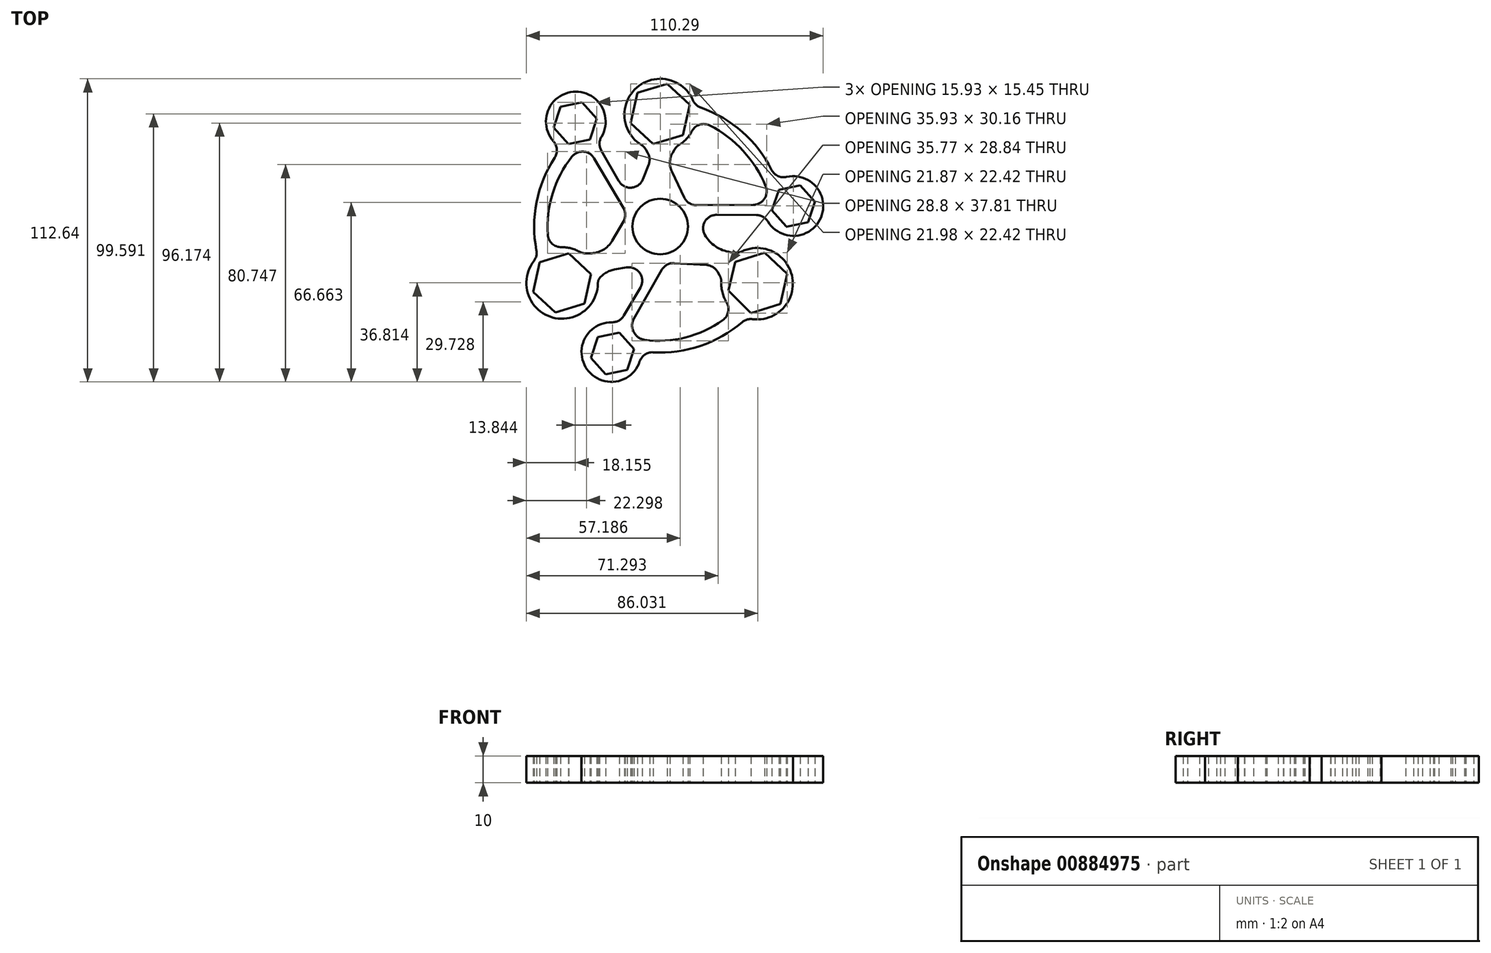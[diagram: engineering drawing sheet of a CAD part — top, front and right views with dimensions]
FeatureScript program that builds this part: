
annotation { "Feature Type Name" : "Feature", "Feature Type Description" : "" }
export const myFeature = defineFeature(function(context is Context, id is Id, definition is map)
    precondition{}
    {
        {
            var Q0;
            Q0=qCreatedBy(makeId("Top.planeOp"),FACE);
            var sketch = newSketch(context, id + "F0", { "sketchPlane" : qUnion([Q0])});
            skCircle(sketch, "E0", {"center": v(0, 0) * mm, "radius": 10.34 * mm});
            skLineSegment(sketch, "E1", {"start": v(16.56, -3.08) * mm, "end": v(16.6, -3.15) * mm});
            skLineSegment(sketch, "E2", {"start": v(21.4, -16.95) * mm, "end": v(22.04, -18.04) * mm});
            skLineSegment(sketch, "E3.1.0", {"start": v(4.6, 27.4) * mm, "end": v(5.25, 28.52) * mm});
            skLineSegment(sketch, "E3.1.1", {"start": v(-6.37, 17.62) * mm, "end": v(-4.26, 23.1) * mm});
            skLineSegment(sketch, "E3.2.0", {"start": v(-26.02, -9.98) * mm, "end": v(-27.6, -9.98) * mm});
            skLineSegment(sketch, "E3.2.1", {"start": v(-12.57, -15.21) * mm, "end": v(-16.95, -16) * mm});
            skLineSegment(sketch, "E4", {"start": v(0, -25.85) * mm, "end": v(0, -10.34) * mm, "construction": true});
            skLineSegment(sketch, "E5.MirrorCS", {"start": v(-13.7, 1.87) * mm, "end": v(-17.8, -5.24) * mm});
            skLineSegment(sketch, "E6.1.0", {"start": v(26.05, -9.53) * mm, "end": v(27.33, -9.72) * mm});
            skLineSegment(sketch, "E6.1.1", {"start": v(5.2, -13.6) * mm, "end": v(17.15, -14.32) * mm});
            skLineSegment(sketch, "E6.2.0", {"start": v(-4.6, 27.4) * mm, "end": v(-5.25, 28.52) * mm});
            skLineSegment(sketch, "E6.2.1", {"start": v(8.96, 10.77) * mm, "end": v(4.33, 20.43) * mm});
            skPoint(sketch, "E7", {"position": v(2.46, 10.04) * mm});
            skPoint(sketch, "E8", {"position": v(-2.46, 10.04) * mm});
            skPoint(sketch, "E9", {"position": v(7.46, 7.15) * mm});
            skPoint(sketch, "E10", {"position": v(9.92, 2.9) * mm});
            skPoint(sketch, "E11", {"position": v(-7.46, 7.15) * mm});
            skPoint(sketch, "E12", {"position": v(-9.92, 2.9) * mm});
            skPoint(sketch, "E13", {"position": v(9.92, -2.9) * mm});
            skPoint(sketch, "E14", {"position": v(7.46, -7.15) * mm});
            skPoint(sketch, "E15", {"position": v(-7.46, -7.15) * mm});
            skPoint(sketch, "E16", {"position": v(-9.92, -2.9) * mm});
            skPoint(sketch, "E17", {"position": v(-2.46, 4.26) * mm});
            skPoint(sketch, "E18", {"position": v(2.46, 4.26) * mm});
            skPoint(sketch, "E19", {"position": v(2.46, -4.26) * mm});
            skPoint(sketch, "E20", {"position": v(-2.46, -4.26) * mm});
            skPoint(sketch, "E21", {"position": v(-4.92, 0) * mm});
            skPoint(sketch, "E22", {"position": v(4.92, 0) * mm});
            skPoint(sketch, "E23", {"position": v(-2.46, 5.46) * mm});
            skPoint(sketch, "E24", {"position": v(2.46, 5.46) * mm});
            skLineSegment(sketch, "E25.2.0", {"start": v(0.55, -16.12) * mm, "end": v(-9.8, -34.32) * mm});
            skLineSegment(sketch, "E25.2.1", {"start": v(-7.37, -22.66) * mm, "end": v(-13.47, -33.1) * mm});
            skLineSegment(sketch, "E26.trimOffspring", {"start": v(0, 10.34) * mm, "end": v(0, 30.35) * mm, "construction": true});
            skPoint(sketch, "E27.third.point", {"position": v(-26.64, -15.38) * mm});
            skPoint(sketch, "E28.third.point", {"position": v(0, 30.35) * mm});
            skPoint(sketch, "E29.third.point", {"position": v(26.28, -15.18) * mm});
            skPoint(sketch, "E30.end.orphan", {"position": v(-26.74, -20.71) * mm});
            skPoint(sketch, "E31.orphan", {"position": v(31.3, -15.18) * mm});
            skPoint(sketch, "E32.orphan", {"position": v(26.74, -20.71) * mm});
            skPoint(sketch, "E33.orphan", {"position": v(-2.51, 34.7) * mm});
            skLineSegment(sketch, "E34.0", {"start": v(-28.18, -28.67) * mm, "end": v(-38.97, -32) * mm});
            skLineSegment(sketch, "E34.1", {"start": v(-38.97, -32) * mm, "end": v(-47.24, -24.3) * mm});
            skLineSegment(sketch, "E34.2", {"start": v(-47.24, -24.3) * mm, "end": v(-44.71, -13.3) * mm});
            skLineSegment(sketch, "E34.3", {"start": v(-44.71, -13.3) * mm, "end": v(-33.92, -9.98) * mm});
            skLineSegment(sketch, "E34.4", {"start": v(-33.92, -9.98) * mm, "end": v(-25.65, -17.67) * mm});
            skLineSegment(sketch, "E34.5", {"start": v(-25.65, -17.67) * mm, "end": v(-28.18, -28.67) * mm});
            skLineSegment(sketch, "E35.1.0", {"start": v(33.67, -32.13) * mm, "end": v(25.37, -23.8) * mm});
            skLineSegment(sketch, "E35.1.1", {"start": v(25.37, -23.8) * mm, "end": v(27.82, -13.1) * mm});
            skLineSegment(sketch, "E35.1.2", {"start": v(27.82, -13.1) * mm, "end": v(38.81, -9.72) * mm});
            skLineSegment(sketch, "E35.1.3", {"start": v(38.81, -9.72) * mm, "end": v(47.24, -17.55) * mm});
            skLineSegment(sketch, "E35.1.4", {"start": v(47.24, -17.55) * mm, "end": v(44.67, -28.76) * mm});
            skLineSegment(sketch, "E35.1.5", {"start": v(44.67, -28.76) * mm, "end": v(33.67, -32.13) * mm});
            skLineSegment(sketch, "E35.2.0", {"start": v(11, 45.23) * mm, "end": v(8.42, 34.02) * mm});
            skLineSegment(sketch, "E35.2.1", {"start": v(8.42, 34.02) * mm, "end": v(-2.57, 30.64) * mm});
            skLineSegment(sketch, "E35.2.2", {"start": v(-2.57, 30.64) * mm, "end": v(-11, 38.47) * mm});
            skLineSegment(sketch, "E35.2.3", {"start": v(-11, 38.47) * mm, "end": v(-8.42, 49.68) * mm});
            skLineSegment(sketch, "E35.2.4", {"start": v(-8.42, 49.68) * mm, "end": v(2.57, 53.06) * mm});
            skLineSegment(sketch, "E35.2.5", {"start": v(2.57, 53.06) * mm, "end": v(11, 45.23) * mm});
            skArc(sketch, "E36.0", {"start": v(-30.01, -9.36) * mm, "mid": v(-33.24, -8.1) * mm, "end": v(-36.68, -7.7) * mm});
            skArc(sketch, "E37.1.0", {"start": v(22.7, -20.74) * mm, "mid": v(23.12, -24.58) * mm, "end": v(24.62, -28.14) * mm});
            skArc(sketch, "E37.2.0", {"start": v(6.96, 30.28) * mm, "mid": v(9.71, 32.53) * mm, "end": v(11.77, 35.43) * mm});
            skPoint(sketch, "E37.center", {"position": v(-0.15, -0.21) * mm});
            skPoint(sketch, "E38.orphan", {"position": v(28.18, -28.67) * mm});
            skArc(sketch, "E39.filletArc", {"start": v(-4.26, 23.1) * mm, "mid": v(-3.94, 25.28) * mm, "end": v(-4.6, 27.4) * mm});
            skArc(sketch, "E40.filletArc", {"start": v(4.6, 27.4) * mm, "mid": v(3.6, 23.95) * mm, "end": v(4.33, 20.43) * mm});
            skArc(sketch, "E41.filletArc", {"start": v(16.56, -3.08) * mm, "mid": v(20.57, -7.4) * mm, "end": v(26.05, -9.53) * mm});
            skPoint(sketch, "E42.newPointB", {"position": v(14.67, -5.29) * mm});
            skArc(sketch, "E42.filletArc", {"start": v(21.4, -16.95) * mm, "mid": v(19.6, -15.1) * mm, "end": v(17.15, -14.32) * mm});
            skPoint(sketch, "E43.newPointA", {"position": v(-14.67, -5.29) * mm});
            skArc(sketch, "E43.filletArc", {"start": v(-16.95, -16) * mm, "mid": v(-20.24, -17.25) * mm, "end": v(-22.86, -19.61) * mm});
            skArc(sketch, "E44.filletArc", {"start": v(-26.02, -9.98) * mm, "mid": v(-21.28, -8.71) * mm, "end": v(-17.8, -5.24) * mm});
            skPoint(sketch, "E45.orphan", {"position": v(6.09, -6.37) * mm});
            skLineSegment(sketch, "E46.1.0", {"start": v(20.95, 4.35) * mm, "end": v(35.75, 4.28) * mm});
            skLineSegment(sketch, "E46.1.1", {"start": v(13.5, 7.93) * mm, "end": v(34.59, 8.08) * mm});
            skLineSegment(sketch, "E46.2.0", {"start": v(-15.38, 16.94) * mm, "end": v(-21.87, 28.32) * mm});
            skLineSegment(sketch, "E46.2.1", {"start": v(-13.72, 6.9) * mm, "end": v(-24.56, 25.37) * mm});
            skPoint(sketch, "E46.center", {"position": v(0.06, -0.37) * mm});
            skPoint(sketch, "E47.third.point", {"position": v(-38.87, 42.04) * mm});
            skLineSegment(sketch, "E48.0", {"start": v(-26.17, 32.36) * mm, "end": v(-34.13, 30.71) * mm});
            skLineSegment(sketch, "E48.1", {"start": v(-34.13, 30.71) * mm, "end": v(-39.54, 36.79) * mm});
            skLineSegment(sketch, "E48.2", {"start": v(-39.54, 36.79) * mm, "end": v(-36.98, 44.51) * mm});
            skLineSegment(sketch, "E48.3", {"start": v(-36.98, 44.51) * mm, "end": v(-29.02, 46.16) * mm});
            skLineSegment(sketch, "E48.4", {"start": v(-29.02, 46.16) * mm, "end": v(-23.6, 40.08) * mm});
            skLineSegment(sketch, "E48.5", {"start": v(-23.6, 40.08) * mm, "end": v(-26.17, 32.36) * mm});
            skLineSegment(sketch, "E49.1.0", {"start": v(-23.14, -41.09) * mm, "end": v(-15.17, -39.44) * mm});
            skLineSegment(sketch, "E49.1.1", {"start": v(-25.7, -48.81) * mm, "end": v(-23.14, -41.09) * mm});
            skLineSegment(sketch, "E49.1.2", {"start": v(-20.29, -54.89) * mm, "end": v(-25.7, -48.81) * mm});
            skLineSegment(sketch, "E49.1.3", {"start": v(-12.32, -53.24) * mm, "end": v(-20.29, -54.89) * mm});
            skLineSegment(sketch, "E49.1.4", {"start": v(-9.76, -45.52) * mm, "end": v(-12.32, -53.24) * mm});
            skLineSegment(sketch, "E49.1.5", {"start": v(-15.17, -39.44) * mm, "end": v(-9.76, -45.52) * mm});
            skLineSegment(sketch, "E49.2.0", {"start": v(46.92, -0.1) * mm, "end": v(41.51, 5.98) * mm});
            skLineSegment(sketch, "E49.2.1", {"start": v(54.89, 1.55) * mm, "end": v(46.92, -0.1) * mm});
            skLineSegment(sketch, "E49.2.2", {"start": v(57.45, 9.27) * mm, "end": v(54.89, 1.55) * mm});
            skLineSegment(sketch, "E49.2.3", {"start": v(52.04, 15.35) * mm, "end": v(57.45, 9.27) * mm});
            skLineSegment(sketch, "E49.2.4", {"start": v(44.07, 13.7) * mm, "end": v(52.04, 15.35) * mm});
            skLineSegment(sketch, "E49.2.5", {"start": v(41.51, 5.98) * mm, "end": v(44.07, 13.7) * mm});
            skArc(sketch, "E49.2.6", {"start": v(46.81, -0.06) * mm, "mid": v(46.87, -0.08) * mm, "end": v(46.92, -0.1) * mm});
            skArc(sketch, "E50.trimOffspring", {"start": v(46.81, -0.06) * mm, "mid": v(46.81, -0.02) * mm, "end": v(46.81, 0.02) * mm});
            skArc(sketch, "E51.trimOffspring", {"start": v(-2.6, -46.74) * mm, "mid": v(14.98, -44.35) * mm, "end": v(30.4, -35.6) * mm});
            skArc(sketch, "E52.trimOffspring", {"start": v(-5.84, -42.1) * mm, "mid": v(9.42, -41.24) * mm, "end": v(23.27, -34.78) * mm});
            skArc(sketch, "E53.trimOffspring", {"start": v(-32.8, 25.92) * mm, "mid": v(-39.95, 12.28) * mm, "end": v(-41.76, -3.02) * mm});
            skPoint(sketch, "E54.visualSharp", {"position": v(5.94, 29.71) * mm});
            skArc(sketch, "E54.filletArc", {"start": v(6.96, 30.28) * mm, "mid": v(6, 29.51) * mm, "end": v(5.25, 28.52) * mm});
            skPoint(sketch, "E55.visualSharp", {"position": v(-5.94, 29.71) * mm});
            skArc(sketch, "E55.filletArc", {"start": v(-5.25, 28.52) * mm, "mid": v(-6, 29.51) * mm, "end": v(-6.96, 30.28) * mm});
            skPoint(sketch, "E56.visualSharp", {"position": v(28.98, -9.96) * mm});
            skArc(sketch, "E56.filletArc", {"start": v(27.33, -9.72) * mm, "mid": v(28.8, -9.71) * mm, "end": v(30.22, -9.28) * mm});
            skPoint(sketch, "E57.visualSharp", {"position": v(-29, -9.98) * mm});
            skArc(sketch, "E57.filletArc", {"start": v(-30.01, -9.36) * mm, "mid": v(-28.84, -9.82) * mm, "end": v(-27.6, -9.98) * mm});
            skPoint(sketch, "E58.visualSharp", {"position": v(-23.19, -20.04) * mm});
            skArc(sketch, "E58.filletArc", {"start": v(-22.86, -19.61) * mm, "mid": v(-23.07, -20.4) * mm, "end": v(-23.16, -21.23) * mm});
            skPoint(sketch, "E59.visualSharp", {"position": v(22.82, -19.4) * mm});
            skArc(sketch, "E59.filletArc", {"start": v(22.7, -20.74) * mm, "mid": v(22.56, -19.34) * mm, "end": v(22.04, -18.04) * mm});
            skArc(sketch, "E60.trimOffspring", {"start": v(-46.94, -12.83) * mm, "mid": v(-40.87, -33.52) * mm, "end": v(-23.16, -21.23) * mm});
            skArc(sketch, "E61.trimOffspring", {"start": v(34.3, -34.43) * mm, "mid": v(49.1, -19.13) * mm, "end": v(30.22, -9.28) * mm});
            skArc(sketch, "E62.trimOffspring", {"start": v(12.18, 46.92) * mm, "mid": v(-8.72, 51.64) * mm, "end": v(-6.96, 30.28) * mm});
            skPoint(sketch, "E63.visualSharp", {"position": v(13.18, 39.86) * mm});
            skArc(sketch, "E63.filletArc", {"start": v(18.49, 37.55) * mm, "mid": v(14.7, 37.87) * mm, "end": v(11.77, 35.43) * mm});
            skPoint(sketch, "E64.visualSharp", {"position": v(-41.04, -8.52) * mm});
            skArc(sketch, "E64.filletArc", {"start": v(-41.76, -3.02) * mm, "mid": v(-40.15, -6.38) * mm, "end": v(-36.68, -7.7) * mm});
            skPoint(sketch, "E65.visualSharp", {"position": v(27.38, -31.38) * mm});
            skArc(sketch, "E65.filletArc", {"start": v(23.27, -34.78) * mm, "mid": v(25.24, -31.72) * mm, "end": v(24.62, -28.14) * mm});
            skArc(sketch, "E66.trimOffspring", {"start": v(39.18, 14.98) * mm, "mid": v(30.84, 28.1) * mm, "end": v(18.49, 37.55) * mm});
            skArc(sketch, "E67", {"start": v(40, 1.88) * mm, "mid": v(59.69, 3.32) * mm, "end": v(46.98, 18.42) * mm});
            skArc(sketch, "E68.1.0", {"start": v(-21.82, 33.36) * mm, "mid": v(-32.38, 50.07) * mm, "end": v(-39.63, 31.68) * mm});
            skArc(sketch, "E68.2.0", {"start": v(-17.9, -35.58) * mm, "mid": v(-27.2, -53.05) * mm, "end": v(-7.62, -50.16) * mm});
            skPoint(sketch, "E69.orphan", {"position": v(41.36, 8.13) * mm});
            skArc(sketch, "E70.trimOffspring", {"start": v(41.4, 21.05) * mm, "mid": v(30.5, 35.17) * mm, "end": v(15.1, 44.2) * mm});
            skArc(sketch, "E71.filletArc", {"start": v(34.59, 8.08) * mm, "mid": v(38.71, 10.3) * mm, "end": v(39.18, 14.98) * mm});
            skPoint(sketch, "E72.visualSharp", {"position": v(43.27, 16.8) * mm});
            skArc(sketch, "E72.filletArc", {"start": v(41.4, 21.05) * mm, "mid": v(43.73, 18.77) * mm, "end": v(46.98, 18.42) * mm});
            skPoint(sketch, "E73.visualSharp", {"position": v(38.92, 4.27) * mm});
            skArc(sketch, "E73.filletArc", {"start": v(40, 1.88) * mm, "mid": v(38.2, 3.63) * mm, "end": v(35.75, 4.28) * mm});
            skPoint(sketch, "E74.visualSharp", {"position": v(10.33, 7.9) * mm});
            skArc(sketch, "E74.filletArc", {"start": v(8.96, 10.77) * mm, "mid": v(10.82, 8.69) * mm, "end": v(13.5, 7.93) * mm});
            skPoint(sketch, "E75.visualSharp", {"position": v(12.25, 4.4) * mm});
            skArc(sketch, "E75.filletArc", {"start": v(20.95, 4.35) * mm, "mid": v(16.6, 1.86) * mm, "end": v(16.6, -3.15) * mm});
            skPoint(sketch, "E76.visualSharp", {"position": v(-12.25, 4.4) * mm});
            skArc(sketch, "E76.filletArc", {"start": v(-13.7, 1.87) * mm, "mid": v(-13.03, 4.39) * mm, "end": v(-13.72, 6.9) * mm});
            skPoint(sketch, "E77.visualSharp", {"position": v(-10.16, 7.8) * mm});
            skArc(sketch, "E77.filletArc", {"start": v(-15.38, 16.94) * mm, "mid": v(-10.66, 14.44) * mm, "end": v(-6.37, 17.62) * mm});
            skPoint(sketch, "E78.visualSharp", {"position": v(2.09, -13.4) * mm});
            skArc(sketch, "E78.filletArc", {"start": v(5.2, -13.6) * mm, "mid": v(2.51, -14.2) * mm, "end": v(0.55, -16.12) * mm});
            skPoint(sketch, "E79.visualSharp", {"position": v(-1.91, -13.3) * mm});
            skArc(sketch, "E79.filletArc", {"start": v(-7.37, -22.66) * mm, "mid": v(-7.6, -17.27) * mm, "end": v(-12.57, -15.21) * mm});
            skArc(sketch, "E80.trimOffspring", {"start": v(-39.18, 25.62) * mm, "mid": v(-45.93, 9.06) * mm, "end": v(-45.97, -8.82) * mm});
            skPoint(sketch, "E81.orphan", {"position": v(-27.95, 31.15) * mm});
            skArc(sketch, "E82.trimOffspring", {"start": v(-9.2, -40.1) * mm, "mid": v(-9.3, -39.98) * mm, "end": v(-9.39, -39.86) * mm});
            skPoint(sketch, "E83.visualSharp", {"position": v(-11.68, -37.65) * mm});
            skArc(sketch, "E83.filletArc", {"start": v(-9.8, -34.32) * mm, "mid": v(-10.43, -37.15) * mm, "end": v(-9.39, -39.86) * mm});
            skPoint(sketch, "E84.visualSharp", {"position": v(-8.22, -41.7) * mm});
            skArc(sketch, "E84.filletArc", {"start": v(-9.2, -40.1) * mm, "mid": v(-7.73, -41.44) * mm, "end": v(-5.84, -42.1) * mm});
            skArc(sketch, "E85.filletArc", {"start": v(-24.56, 25.37) * mm, "mid": v(-28.54, 27.83) * mm, "end": v(-32.8, 25.92) * mm});
            skPoint(sketch, "E86.orphan", {"position": v(-16.95, -39.07) * mm});
            skPoint(sketch, "E87.orphan", {"position": v(-13.24, -40.38) * mm});
            skPoint(sketch, "E88.visualSharp", {"position": v(-15.15, -35.99) * mm});
            skArc(sketch, "E88.filletArc", {"start": v(-17.9, -35.58) * mm, "mid": v(-15.34, -34.95) * mm, "end": v(-13.47, -33.1) * mm});
            skPoint(sketch, "E89.visualSharp", {"position": v(-7.06, -46.28) * mm});
            skArc(sketch, "E89.filletArc", {"start": v(-2.6, -46.74) * mm, "mid": v(-5.69, -47.6) * mm, "end": v(-7.62, -50.16) * mm});
            skArc(sketch, "E90.trimOffspring", {"start": v(44.5, -28.8) * mm, "mid": v(44.6, -28.7) * mm, "end": v(44.7, -28.6) * mm});
            skPoint(sketch, "E91.orphan", {"position": v(42.07, 4.25) * mm});
            skPoint(sketch, "E92.orphan", {"position": v(-24.95, 33.7) * mm});
            skPoint(sketch, "E93.visualSharp", {"position": v(32.19, -33.99) * mm});
            skArc(sketch, "E93.filletArc", {"start": v(34.3, -34.43) * mm, "mid": v(32.23, -34.6) * mm, "end": v(30.4, -35.6) * mm});
            skPoint(sketch, "E94.visualSharp", {"position": v(-45.45, -11.21) * mm});
            skArc(sketch, "E94.filletArc", {"start": v(-46.94, -12.83) * mm, "mid": v(-46.02, -10.93) * mm, "end": v(-45.97, -8.82) * mm});
            skPoint(sketch, "E95.visualSharp", {"position": v(-36.55, 29.25) * mm});
            skArc(sketch, "E95.filletArc", {"start": v(-39.18, 25.62) * mm, "mid": v(-38.38, 28.72) * mm, "end": v(-39.63, 31.68) * mm});
            skPoint(sketch, "E96.visualSharp", {"position": v(-23.52, 31.2) * mm});
            skArc(sketch, "E96.filletArc", {"start": v(-21.82, 33.36) * mm, "mid": v(-22.53, 30.84) * mm, "end": v(-21.87, 28.32) * mm});
            skPoint(sketch, "E97.visualSharp", {"position": v(12.87, 44.93) * mm});
            skArc(sketch, "E97.filletArc", {"start": v(12.18, 46.92) * mm, "mid": v(13.36, 45.25) * mm, "end": v(15.1, 44.2) * mm});
            skSolve(sketch);
        }
        {
            var Q0;
            Q0 = qSketchRegion(id + "F0", true);
            extrude(context, id + "F1", {"entities" : qUnion([Q0]), "depth" : 10 * mm, "offsetDistance" : 25 * mm});
        }
    });
